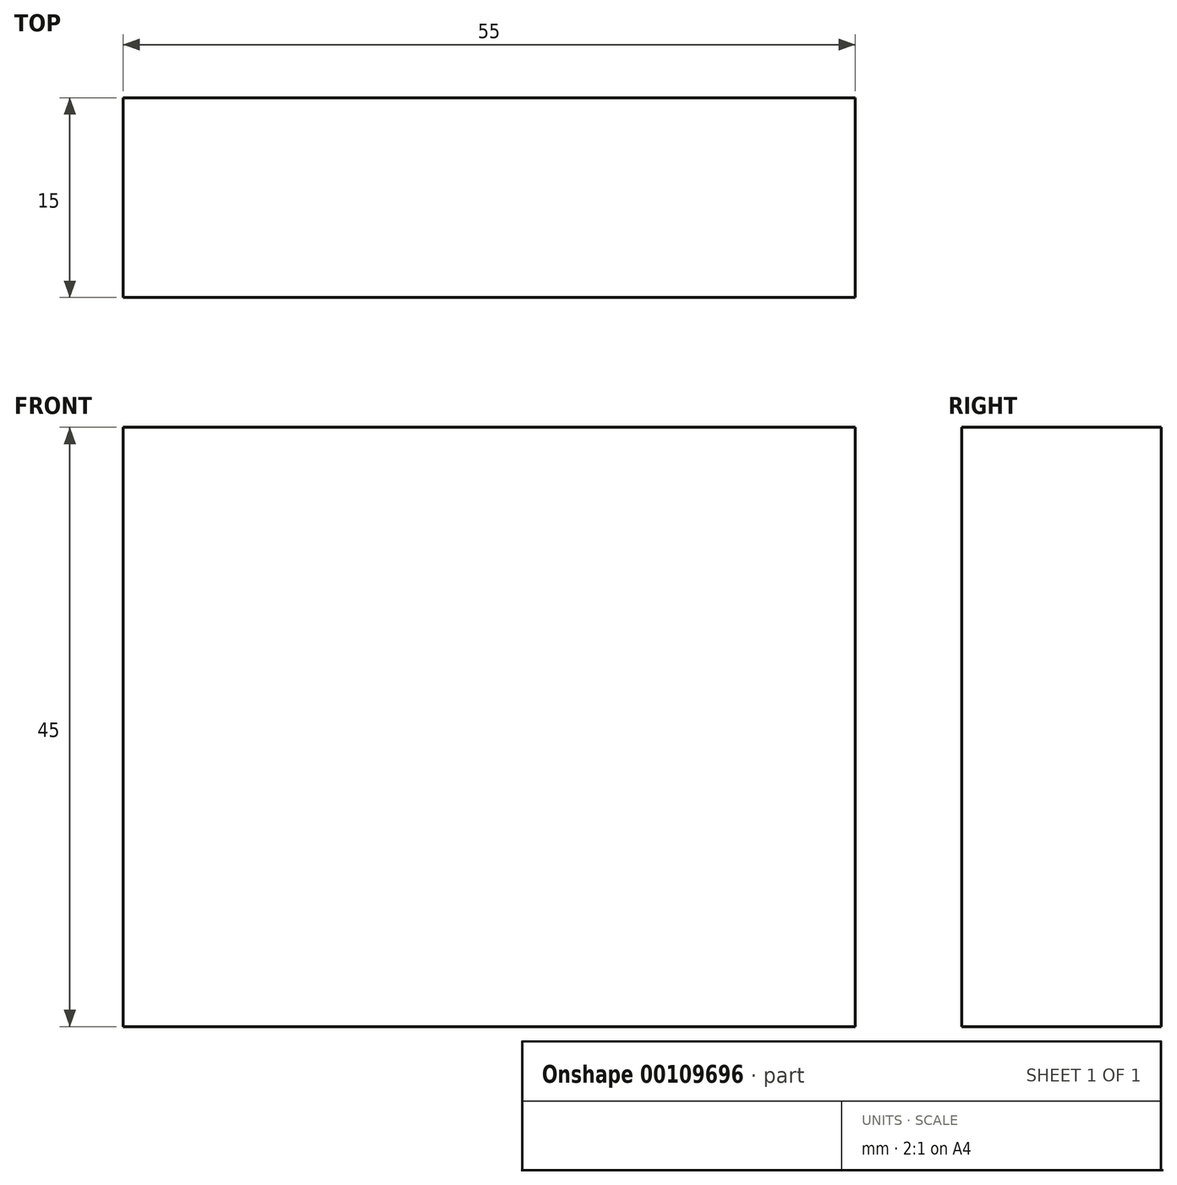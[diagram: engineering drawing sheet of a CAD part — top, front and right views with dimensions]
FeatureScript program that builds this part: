
annotation { "Feature Type Name" : "Feature", "Feature Type Description" : "" }
export const myFeature = defineFeature(function(context is Context, id is Id, definition is map)
    precondition{}
    {
        {
            var Q0;
            Q0=qCreatedBy(makeId("Front.planeOp"),FACE);
            var sketch = newSketch(context, id + "F0", { "sketchPlane" : qUnion([Q0])});
            skLineSegment(sketch, "E0", {"start": v(0, 0) * mm, "end": v(55, 0) * mm});
            skLineSegment(sketch, "E1", {"start": v(0, 0) * mm, "end": v(0, 45) * mm});
            skLineSegment(sketch, "E2", {"start": v(0, 45) * mm, "end": v(55, 45) * mm});
            skLineSegment(sketch, "E3", {"start": v(55, 45) * mm, "end": v(55, 0) * mm});
            skSolve(sketch);
        }
        {
            var Q0;
            Q0 = qSketchRegion(id + "F0", true);
            var Q1;
            Q1=makeQuery(id+"F0.imprint","IMPRINT",FACE,{"disambiguationData":[TD([[makeQuery(id+"F0.imprint","IMPRINT",EDGE,{"derivedFrom":sQuery(id+"F0.wireOp",EDGE,"E0")}),1.0]])]});
            extrude(context, id + "F1", {"entities" : qUnion([Q0, Q1]), "depth" : 15 * mm});
        }
    });
